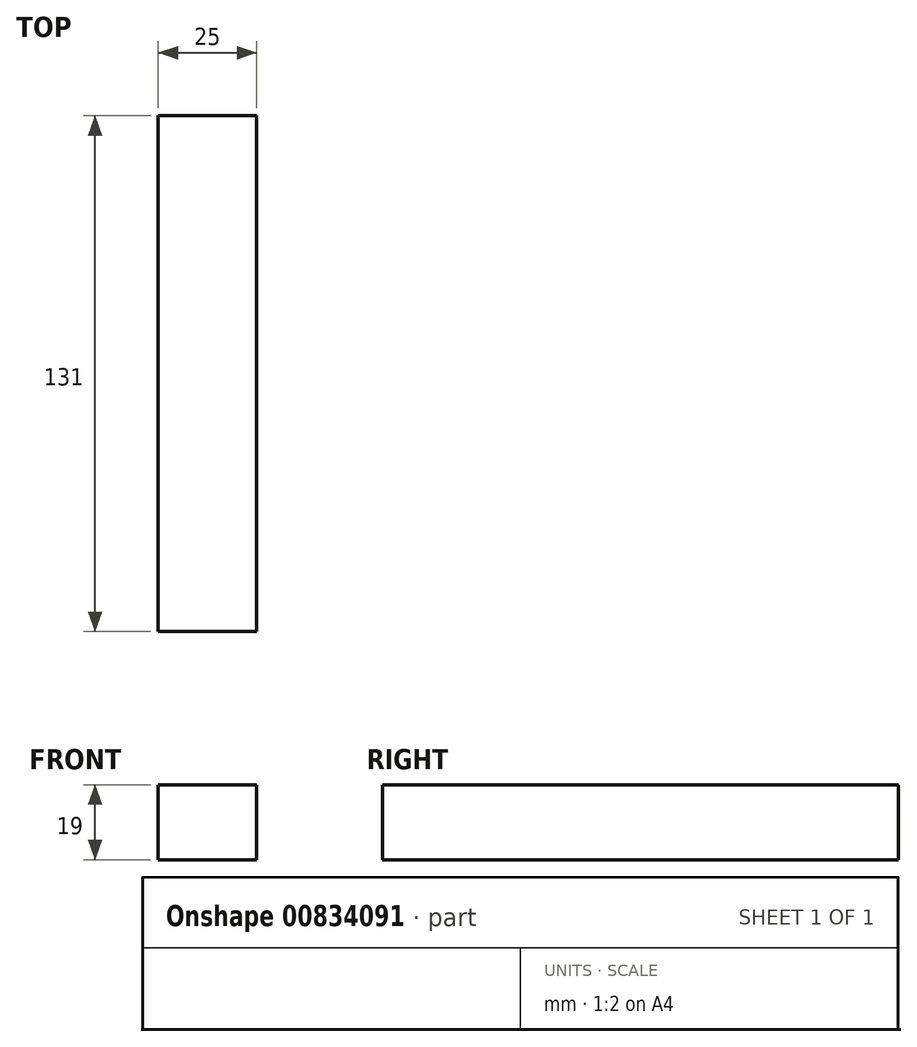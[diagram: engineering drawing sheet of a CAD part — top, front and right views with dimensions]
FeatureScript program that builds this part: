
annotation { "Feature Type Name" : "Feature", "Feature Type Description" : "" }
export const myFeature = defineFeature(function(context is Context, id is Id, definition is map)
    precondition{}
    {
        {
            var Q0;
            Q0=qCreatedBy(makeId("Top.planeOp"),FACE);
            var sketch = newSketch(context, id + "F0", { "sketchPlane" : qUnion([Q0])});
            skLineSegment(sketch, "E0.bottom", {"start": v(12.5, 65.5) * mm, "end": v(-12.5, 65.5) * mm});
            skLineSegment(sketch, "E0.top", {"start": v(12.5, -65.5) * mm, "end": v(-12.5, -65.5) * mm});
            skLineSegment(sketch, "E0.left", {"start": v(12.5, 65.5) * mm, "end": v(12.5, -65.5) * mm});
            skLineSegment(sketch, "E0.right", {"start": v(-12.5, 65.5) * mm, "end": v(-12.5, -65.5) * mm});
            skPoint(sketch, "E0.middle", {"position": v(0, 0) * mm});
            skSolve(sketch);
        }
        {
            var Q0;
            Q0 = qSketchRegion(id + "F0", true);
            extrude(context, id + "F1", {"entities" : qUnion([Q0]), "depth" : 19 * mm, "offsetDistance" : 25 * mm});
        }
    });
